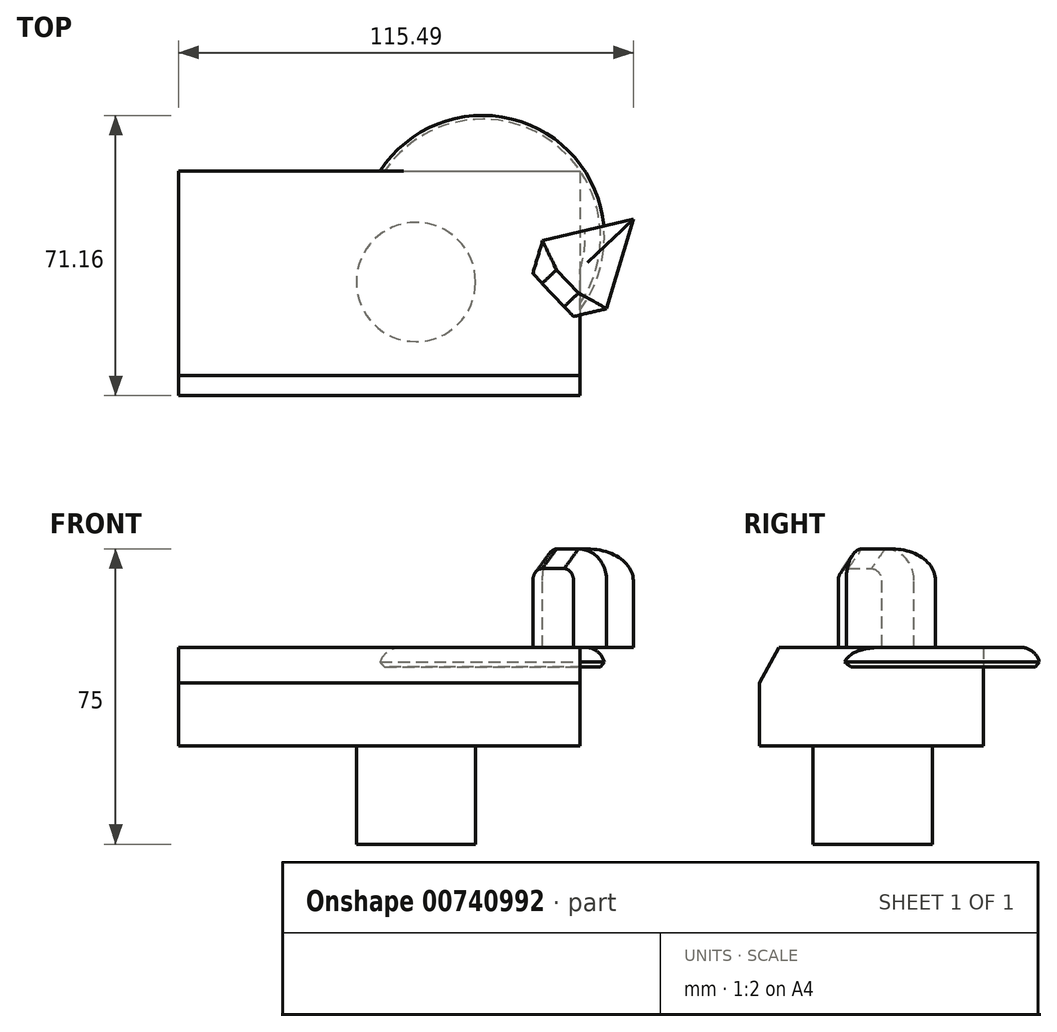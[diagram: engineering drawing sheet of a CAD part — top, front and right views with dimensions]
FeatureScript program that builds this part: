
annotation { "Feature Type Name" : "Feature", "Feature Type Description" : "" }
export const myFeature = defineFeature(function(context is Context, id is Id, definition is map)
    precondition{}
    {
        {
            var Q0;
            Q0=qCreatedBy(makeId("Top.planeOp"),FACE);
            var sketch = newSketch(context, id + "F0", { "sketchPlane" : qUnion([Q0])});
            skLineSegment(sketch, "E0.bottom", {"start": v(-47.7, 26.82) * mm, "end": v(54.2, 26.82) * mm});
            skLineSegment(sketch, "E0.top", {"start": v(-47.7, -30.15) * mm, "end": v(54.2, -30.15) * mm});
            skLineSegment(sketch, "E0.left", {"start": v(-47.7, 26.82) * mm, "end": v(-47.7, -30.15) * mm});
            skLineSegment(sketch, "E0.right", {"start": v(54.2, 26.82) * mm, "end": v(54.2, -30.15) * mm});
            skSolve(sketch);
        }
        {
            var Q0;
            Q0=makeQuery(id+"F0.imprint","IMPRINT",FACE,{"disambiguationData":[TD([[makeQuery(id+"F0.imprint","IMPRINT",EDGE,{"derivedFrom":sQuery(id+"F0.wireOp",EDGE,"E0.bottom")}),-1.0]])]});
            extrude(context, id + "F1", {"entities" : qUnion([Q0]), "endBound" : BoundingType.SYMMETRIC, "depth" : 25 * mm, "offsetDistance" : 25 * mm});
        }
        {
            var Q0;
            Q0=makeQuery(id+"F1.opExtrude","CAP_EDGE",EDGE,{"disambiguationData":[OSD([sQuery(id+"F0.wireOp",EDGE,"E0.top")])],"isStart":false});
            chamfer(context, id + "F2", {"entities" : qUnion([Q0]), "chamferType" : ChamferType.TWO_OFFSETS, "width1" : 5 * mm, "oppositeDirection" : false, "width2" : 9 * mm, "tangentPropagation" : true});
        }
        {
            var Q0;
            Q0=makeQuery(id+"F1.opExtrude","CAP_FACE",FACE,{"disambiguationData":[OSD([sQuery(id+"F0.wireOp",EDGE,"E0.bottom"),sQuery(id+"F0.wireOp",EDGE,"E0.top"),sQuery(id+"F0.wireOp",EDGE,"E0.left"),sQuery(id+"F0.wireOp",EDGE,"E0.right")])],"isStart":false});
            var sketch = newSketch(context, id + "F3", { "sketchPlane" : qUnion([Q0])});
            skCircle(sketch, "E1", {"center": v(29.43, 10.07) * mm, "radius": 31.1 * mm});
            skCircle(sketch, "E2", {"center": v(0, 0) * mm, "radius": 19.88 * mm});
            skSolve(sketch);
        }
        {
            var Q0;
            {var subQ3=sQuery(id+"F3.wireOp",EDGE,"E1");var subQ5=sQuery(id+"F3.wireOp",EDGE,"E2");var subQ8=makeQuery(id+"F3.imprint","INTERSECT",VERTEX,{"disambiguationData":[OD(0.0)],"derivedFrom":[subQ3,subQ5]});Q0=makeQuery(id+"F3.imprint","IMPRINT",FACE,{"disambiguationData":[TD([[makeQuery(id+"F3.imprint","IMPRINT",EDGE,{"disambiguationData":[TD([[subQ8,1.0]])],"derivedFrom":subQ3}),1.0]])]});}
            var Q1;
            {var subQ0=sQuery(id+"F3.wireOp",EDGE,"E1");var subQ1=makeQuery(id+"F1.opExtrude","CAP_EDGE",EDGE,{"disambiguationData":[OSD([sQuery(id+"F0.wireOp",EDGE,"E0.bottom")])],"isStart":false});var subQ2=makeQuery(id+"F3.imprint","INTERSECT",VERTEX,{"derivedFrom":[subQ1,subQ0]});Q1=makeQuery(id+"F3.imprint","IMPRINT",FACE,{"disambiguationData":[TD([[makeQuery(id+"F3.imprint","IMPRINT",EDGE,{"disambiguationData":[TD([[subQ2,1.0]])],"derivedFrom":subQ0}),1.0]])]});}
            extrude(context, id + "F4", {"entities" : qUnion([Q0, Q1]), "operationType" : NewBodyOperationType.ADD, "oppositeDirection" : true, "depth" : 5 * mm, "offsetDistance" : 25 * mm});
        }
        {
            var Q0;
            Q0=makeQuery(id+"F4.opExtrude","CAP_EDGE",EDGE,{"disambiguationData":[OSD([sQuery(id+"F3.wireOp",EDGE,"E1")])],"isStart":true});
            fillet(context, id + "F5", {"entities" : qUnion([Q0]), "radius" : 5 * mm, "tangentPropagation" : true, "allowEdgeOverflow" : false});
        }
        {
            var Q0;
            Q0=makeQuery(id+"F4.boolean.opBoolean","MERGE",FACE,{"derivedFrom":[makeQuery(id+"F1.opExtrude","CAP_FACE",FACE,{"disambiguationData":[OSD([sQuery(id+"F0.wireOp",EDGE,"E0.bottom"),sQuery(id+"F0.wireOp",EDGE,"E0.top"),sQuery(id+"F0.wireOp",EDGE,"E0.left"),sQuery(id+"F0.wireOp",EDGE,"E0.right")])],"isStart":false}),makeQuery(id+"F4.opExtrude","CAP_FACE",FACE,{"disambiguationData":[OSD([sQuery(id+"F3.wireOp",EDGE,"E1"),sQuery(id+"F3.wireOp",EDGE,"E2")])],"isStart":true})]});
            var sketch = newSketch(context, id + "F6", { "sketchPlane" : qUnion([Q0])});
            skCircle(sketch, "E3.cCircle", {"center": v(54.2, 1.8) * mm, "radius": 18.69 * mm, "construction": true});
            skLineSegment(sketch, "E3.0", {"start": v(36.3, 7.15) * mm, "end": v(67.78, 14.63) * mm});
            skLineSegment(sketch, "E3.1", {"start": v(67.78, 14.63) * mm, "end": v(58.52, -16.38) * mm});
            skLineSegment(sketch, "E3.2", {"start": v(58.52, -16.38) * mm, "end": v(36.3, 7.15) * mm});
            skSolve(sketch);
        }
        {
            var Q0;
            {var subQ0=sQuery(id+"F6.wireOp",EDGE,"E3.2");var subQ1=sQuery(id+"F6.wireOp",EDGE,"E3.0");var subQ2=makeQuery(id+"F6.imprint","INTERSECT",VERTEX,{"derivedFrom":[subQ1,subQ0]});Q0=makeQuery(id+"F6.imprint","IMPRINT",FACE,{"disambiguationData":[TD([[makeQuery(id+"F6.imprint","IMPRINT",EDGE,{"disambiguationData":[TD([[subQ2,1.0]])],"derivedFrom":subQ0}),-1.0]])]});}
            var Q1;
            {var subQ8=sQuery(id+"F6.wireOp",EDGE,"E3.1");Q1=makeQuery(id+"F6.imprint","IMPRINT",FACE,{"disambiguationData":[TD([[makeQuery(id+"F6.imprint","IMPRINT",EDGE,{"derivedFrom":subQ8}),-1.0]])]});}
            extrude(context, id + "F7", {"entities" : qUnion([Q0, Q1]), "operationType" : NewBodyOperationType.ADD, "depth" : 25 * mm, "offsetDistance" : 25 * mm});
        }
        {
            var Q0;
            Q0=makeQuery(id+"F7.opExtrude","CAP_EDGE",EDGE,{"disambiguationData":[OSD([sQuery(id+"F6.wireOp",EDGE,"E3.0")])],"isStart":false});
            var Q1;
            Q1=makeQuery(id+"F7.opExtrude","CAP_EDGE",EDGE,{"disambiguationData":[OSD([sQuery(id+"F6.wireOp",EDGE,"E3.1")])],"isStart":false});
            fillet(context, id + "F8", {"entities" : qUnion([Q0, Q1]), "radius" : 8 * mm, "tangentPropagation" : true, "allowEdgeOverflow" : false});
        }
        {
            var Q0;
            Q0=makeQuery(id+"F7.opExtrude","CAP_EDGE",EDGE,{"disambiguationData":[OSD([sQuery(id+"F6.wireOp",EDGE,"E3.2")])],"isStart":false});
            chamfer(context, id + "F9", {"entities" : qUnion([Q0]), "width" : 5 * mm, "tangentPropagation" : true});
        }
        {
            var Q0;
            {var subQ0=sQuery(id+"F3.wireOp",EDGE,"E1");Q0=makeQuery(id+"F5.opFillet","BLEND_EDGE",EDGE,{"blendedFrom":[makeQuery(id+"F4.opExtrude","CAP_EDGE",EDGE,{"disambiguationData":[OSD([subQ0])],"isStart":true}),makeQuery(id+"F4.opExtrude","CAP_FACE",FACE,{"disambiguationData":[OSD([subQ0,sQuery(id+"F3.wireOp",EDGE,"E2")])],"isStart":false})],"blendedInto":[makeQuery(id+"F4.opExtrude","CAP_FACE",FACE,{"disambiguationData":[OSD([subQ0,sQuery(id+"F3.wireOp",EDGE,"E2")])],"isStart":false})]});}
            chamfer(context, id + "F10", {"entities" : qUnion([Q0]), "width" : 1 * mm, "tangentPropagation" : true});
        }
        {
            var Q0;
            Q0=makeQuery(id+"F1.opExtrude","CAP_FACE",FACE,{"disambiguationData":[OSD([sQuery(id+"F0.wireOp",EDGE,"E0.bottom"),sQuery(id+"F0.wireOp",EDGE,"E0.top"),sQuery(id+"F0.wireOp",EDGE,"E0.left"),sQuery(id+"F0.wireOp",EDGE,"E0.right")])],"isStart":true});
            var sketch = newSketch(context, id + "F11", { "sketchPlane" : qUnion([Q0])});
            skLineSegment(sketch, "E4.0", {"start": v(28.3, -26.82) * mm, "end": v(28.3, 30.15) * mm});
            skSolve(sketch);
        }
        {
            var Q0;
            {var subQ0=sQuery(id+"F11.wireOp",EDGE,"E4.0");Q0=makeQuery(id+"F11.imprint","IMPRINT",FACE,{"disambiguationData":[TD([[makeQuery(id+"F11.imprint","IMPRINT",EDGE,{"derivedFrom":subQ0}),1.0]])]});}
            var sketch = newSketch(context, id + "F12", { "sketchPlane" : qUnion([Q0])});
            skCircle(sketch, "E5", {"center": v(12.54, 1.33) * mm, "radius": 15.14 * mm});
            skPoint(sketch, "E5.first.point", {"position": v(0, 9.82) * mm});
            skPoint(sketch, "E5.second.point", {"position": v(27.62, 0) * mm});
            skPoint(sketch, "E5.third.point", {"position": v(0, -7.15) * mm});
            skSolve(sketch);
        }
        {
            var Q0;
            Q0=makeQuery(id+"F12.imprint","IMPRINT",FACE,{"disambiguationData":[TD([[makeQuery(id+"F12.imprint","IMPRINT",EDGE,{"derivedFrom":sQuery(id+"F12.wireOp",EDGE,"E5")}),1.0]])]});
            extrude(context, id + "F13", {"entities" : qUnion([Q0]), "operationType" : NewBodyOperationType.ADD, "depth" : 25 * mm, "offsetDistance" : 25 * mm});
        }
    });
